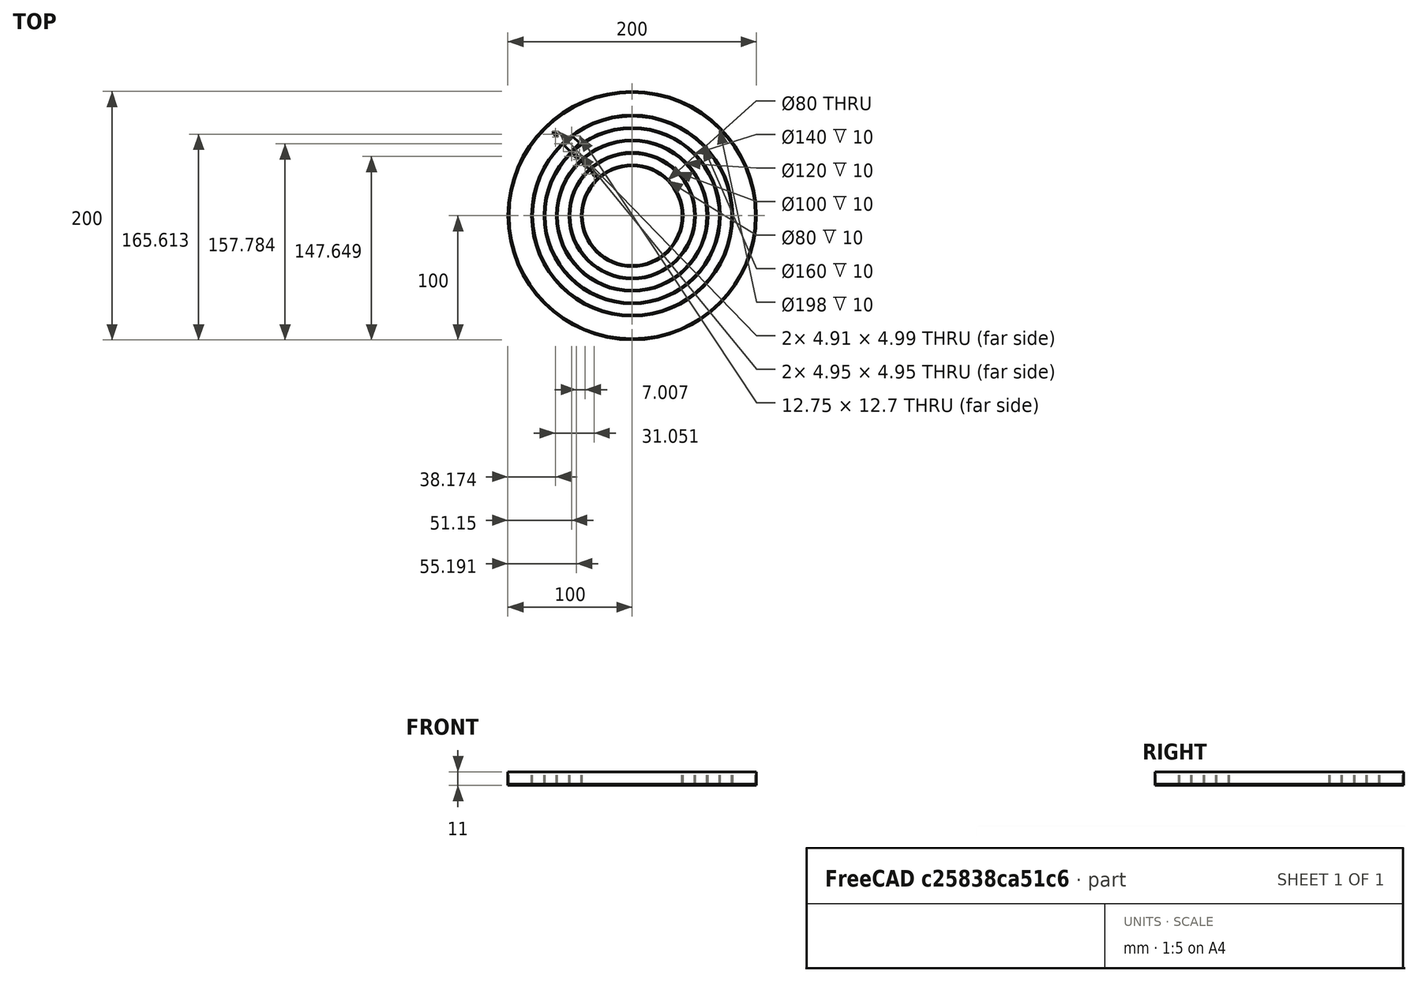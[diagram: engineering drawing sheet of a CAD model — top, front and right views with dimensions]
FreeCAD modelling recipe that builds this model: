
FCSTD DOCUMENT  (FreeCAD 0.18.4R)
Label: orologio
License: All rights reserved
LicenseURL: http://en.wikipedia.org/wiki/All_rights_reserved
objects: Part::Cylinder×17, Part::Cut×15, Part::Box×5
note: 37 computed .brp shape members not serialized (recipe doc carries the construction recipe); baked Part::Feature solids carry a one-line shape summary decoded from their .brp

FEATURE [Part::Cylinder] Cylinder  label="Cilindro"
  Angle = 360
  AttacherType = Attacher::AttachEngine3D
  Height = 10
  Radius = 100
FEATURE [Part::Cylinder] Cylinder001  label="Cilindro001"
  Angle = 360
  AttacherType = Attacher::AttachEngine3D
  Height = 10
  Radius = 99
FEATURE [Part::Cut] Cut
  Base = -> Cylinder
  Tool = -> Cylinder001
FEATURE [Part::Cylinder] Cylinder002  label="Cilindro002"
  Angle = 360
  AttacherType = Attacher::AttachEngine3D
  Height = 10
  Radius = 80
FEATURE [Part::Cylinder] Cylinder003  label="Cilindro003"
  Angle = 360
  AttacherType = Attacher::AttachEngine3D
  Height = 10
  Radius = 81
FEATURE [Part::Cut] Cut001
  Base = -> Cylinder003
  Tool = -> Cylinder002
FEATURE [Part::Cylinder] Cylinder004  label="Cilindro004"
  Angle = 360
  AttacherType = Attacher::AttachEngine3D
  Height = 10
  Radius = 81
FEATURE [Part::Cylinder] Cylinder005  label="Cilindro005"
  Angle = 360
  AttacherType = Attacher::AttachEngine3D
  Height = 10
  Radius = 70
FEATURE [Part::Cut] Cut002
  Base = -> Cylinder004
  Tool = -> Cylinder005
FEATURE [Part::Cylinder] Cylinder006  label="Cilindro006"
  Angle = 360
  AttacherType = Attacher::AttachEngine3D
  Height = 10
  Radius = 71
FEATURE [Part::Cylinder] Cylinder007  label="Cilindro007"
  Angle = 360
  AttacherType = Attacher::AttachEngine3D
  Height = 10
  Radius = 70
FEATURE [Part::Cut] Cut004
  Base = -> Cylinder006
  Tool = -> Cylinder007
FEATURE [Part::Cylinder] Cylinder008  label="Cilindro008"
  Angle = 360
  AttacherType = Attacher::AttachEngine3D
  Height = 10
  Radius = 60
FEATURE [Part::Cylinder] Cylinder009  label="Cilindro009"
  Angle = 360
  AttacherType = Attacher::AttachEngine3D
  Height = 10
  Radius = 61
FEATURE [Part::Cut] Cut005
  Base = -> Cylinder009
  Tool = -> Cylinder008
FEATURE [Part::Cylinder] Cylinder010  label="Cilindro010"
  Angle = 360
  AttacherType = Attacher::AttachEngine3D
  Height = 10
  Radius = 50
FEATURE [Part::Cylinder] Cylinder011  label="Cilindro011"
  Angle = 360
  AttacherType = Attacher::AttachEngine3D
  Height = 10
  Radius = 51
FEATURE [Part::Cut] Cut006
  Base = -> Cylinder011
  Tool = -> Cylinder010
FEATURE [Part::Cylinder] Cylinder012  label="Cilindro012"
  Angle = 360
  AttacherType = Attacher::AttachEngine3D
  Height = 10
  Radius = 40
FEATURE [Part::Cylinder] Cylinder013  label="Cilindro013"
  Angle = 360
  AttacherType = Attacher::AttachEngine3D
  Height = 10
  Radius = 41
FEATURE [Part::Cut] Cut007
  Base = -> Cylinder013
  Tool = -> Cylinder012
FEATURE [Part::Cylinder] Cylinder014  label="Cilindro014"
  Angle = 360
  AttacherType = Attacher::AttachEngine3D
  Height = 10
  Radius = 40
FEATURE [Part::Cylinder] Cylinder015  label="Cilindro015"
  Angle = 360
  AttacherType = Attacher::AttachEngine3D
  Height = 1
  Placement = pos=(0,0,-1) rot=(0,0,1;0rad)
  Radius = 100
FEATURE [Part::Cylinder] Cylinder016  label="Cilindro016"
  Angle = 360
  AttacherType = Attacher::AttachEngine3D
  Height = 1
  Placement = pos=(0,0,-1) rot=(0,0,1;0rad)
  Radius = 40
FEATURE [Part::Cut] Cut009
  Base = -> Cylinder015
  Tool = -> Cylinder016
FEATURE [Part::Box] Box008  label="Cubo008"
  AttacherType = Attacher::AttachEngine3D
  Height = 1
  Length = 10
  Placement = pos=(-49.668,51.4328,-1) rot=(0,0,1;0.767945rad)
  Width = 8
FEATURE [Part::Cut] Cut010
  Base = -> Cut009
  Tool = -> Box008
FEATURE [Part::Box] Box009  label="Cubo009"
  AttacherType = Attacher::AttachEngine3D
  Height = 1
  Length = 2
  Placement = pos=(-43.748,45.1738,-1) rot=(0,0,1;0.785398rad)
  Width = 5
FEATURE [Part::Cut] Cut011
  Base = -> Cut010
  Tool = -> Box009
FEATURE [Part::Box] Box010  label="Cubo010"
  AttacherType = Attacher::AttachEngine3D
  Height = 1
  Length = 2
  Placement = pos=(-36.7407,38.0661,-1) rot=(0,0,-1;5.49779rad)
  Width = 5
FEATURE [Part::Cut] Cut012
  Base = -> Cut011
  Tool = -> Box010
FEATURE [Part::Box] Box011  label="Cubo011"
  AttacherType = Attacher::AttachEngine3D
  Height = 1
  Length = 2
  Placement = pos=(-29.7573,30.9657,-1) rot=(0,0,1;0.767945rad)
  Width = 5
FEATURE [Part::Cut] Cut013
  Base = -> Cut012
  Tool = -> Box011
FEATURE [Part::Box] Box012  label="Cubo012"
  AttacherType = Attacher::AttachEngine3D
  Height = 1
  Length = 2
  Placement = pos=(-60.8085,63.1201,-1) rot=(0,0,1;0.767945rad)
  Width = 5
FEATURE [Part::Cut] Cut014
  Base = -> Cut013
  Tool = -> Box012
FEATURE [Part::Cut] Cut015
  Base = -> Cut014
  Tool = -> Cut002
FEATURE [Part::Cut] Cut016
  Base = -> Cut015
  Tool = -> Cylinder014
